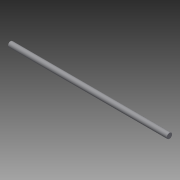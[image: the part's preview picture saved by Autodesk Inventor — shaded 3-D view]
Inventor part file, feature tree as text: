
AUTODESK INVENTOR PART (.ipt)
format: ipt  version: 2015 (Build 190159000, 159)  size: 65,536 bytes
history: native  units: in
note: dims shown in document units (in); Inventor stores cm internally (conversion verified against a paired STEP export)
features: extrude x1, sketch x1
ambient origin geometry x8: Origin, YZ Plane, XZ Plane, XY Plane, X Axis, Y Axis, Z Axis, Center Point
bodies: Solid1 (feature_tree)
feature tree (2):
  extrude  "Extrusion1"  Depth=10.0in TaperAngle=0.0deg
  sketch  "Sketch1"  dims[d0=0.25in d1=10.0in d2=0.0in]
